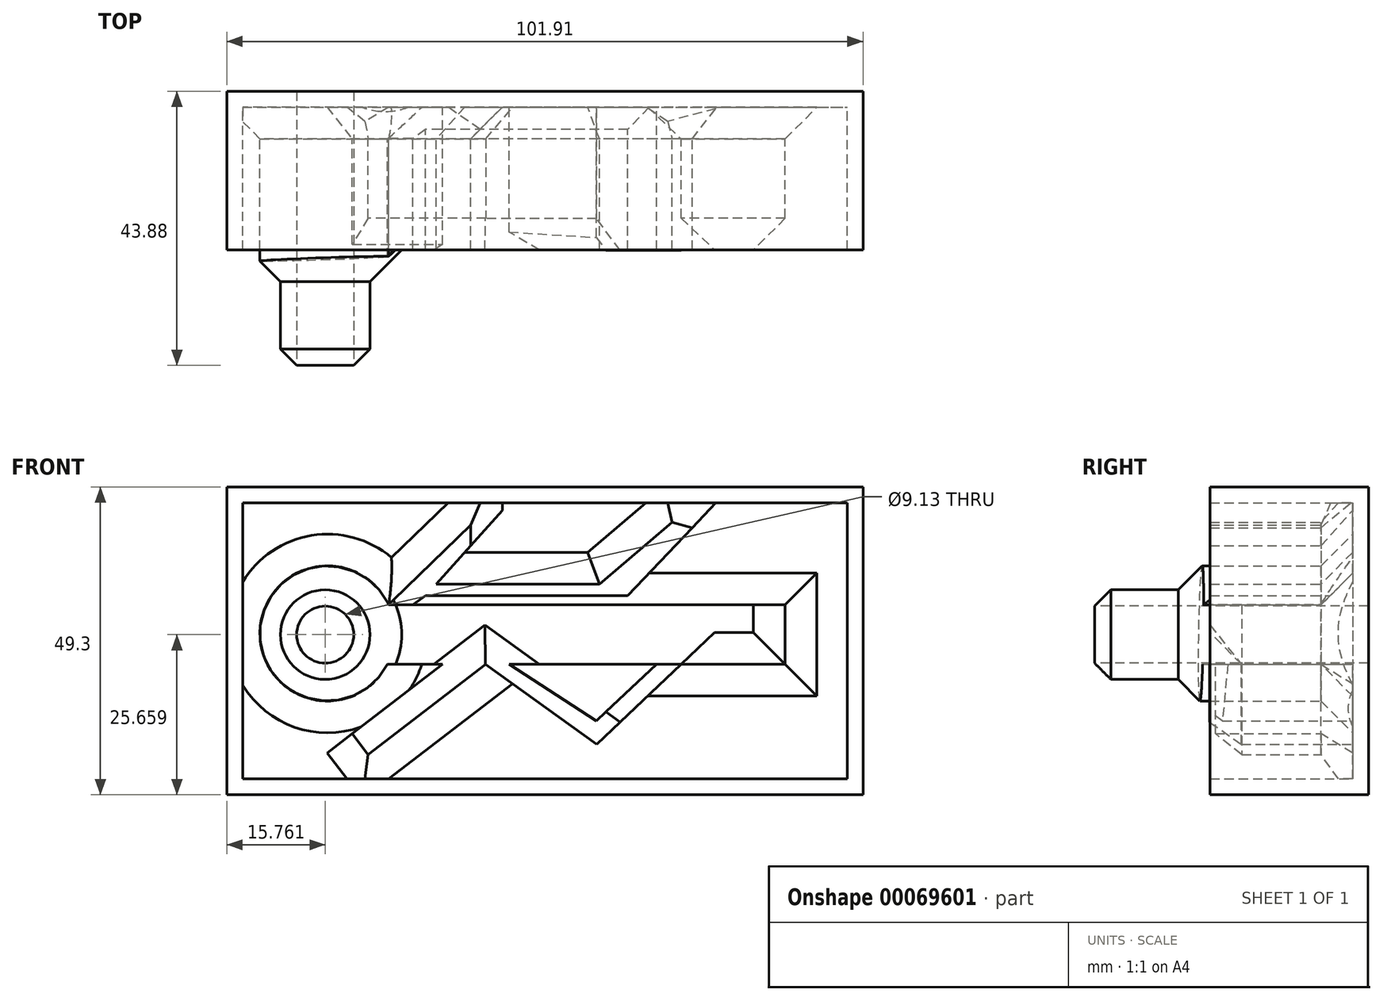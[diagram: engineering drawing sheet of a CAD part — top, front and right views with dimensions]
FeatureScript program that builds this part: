
annotation { "Feature Type Name" : "Feature", "Feature Type Description" : "" }
export const myFeature = defineFeature(function(context is Context, id is Id, definition is map)
    precondition{}
    {
        {
            var Q0;
            Q0=qCreatedBy(makeId("Front.planeOp"),FACE);
            var sketch = newSketch(context, id + "F0", { "sketchPlane" : qUnion([Q0])});
            skLineSegment(sketch, "E0.bottom", {"start": v(-39.04, 53.61) * mm, "end": v(62.87, 53.61) * mm});
            skLineSegment(sketch, "E0.top", {"start": v(-39.04, 4.3) * mm, "end": v(62.87, 4.3) * mm});
            skLineSegment(sketch, "E0.left", {"start": v(-39.04, 53.61) * mm, "end": v(-39.04, 4.3) * mm});
            skLineSegment(sketch, "E0.right", {"start": v(62.87, 53.61) * mm, "end": v(62.87, 4.3) * mm});
            skSolve(sketch);
        }
        {
            var Q0;
            Q0 = qSketchRegion(id + "F0", true);
            extrude(context, id + "F1", {"entities" : qUnion([Q0]), "depth" : 25.4 * mm});
        }
        {
            var Q0;
            Q0=makeQuery(id+"F1.opExtrude","CAP_FACE",FACE,{"disambiguationData":[OSD([sQuery(id+"F0.wireOp",EDGE,"E0.bottom"),sQuery(id+"F0.wireOp",EDGE,"E0.top"),sQuery(id+"F0.wireOp",EDGE,"E0.left"),sQuery(id+"F0.wireOp",EDGE,"E0.right")])],"isStart":false});
            shell(context, id + "F2", {"entities" : qUnion([Q0]), "thickness" : 2.54 * mm});
        }
        {
            var Q0;
            Q0=qCreatedBy(makeId("Front.planeOp"),FACE);
            var sketch = newSketch(context, id + "F3", { "sketchPlane" : qUnion([Q0])});
            skCircle(sketch, "E1", {"center": v(-22.91, 30.15) * mm, "radius": 10.83 * mm});
            skSolve(sketch);
        }
        {
            var Q0;
            Q0 = qSketchRegion(id + "F3", true);
            extrude(context, id + "F4", {"entities" : qUnion([Q0]), "operationType" : NewBodyOperationType.ADD, "depth" : 25.4 * mm});
        }
        {
            var Q0;
            Q0=qCreatedBy(makeId("Front.planeOp"),FACE);
            var sketch = newSketch(context, id + "F5", { "sketchPlane" : qUnion([Q0])});
            skLineSegment(sketch, "E2.bottom", {"start": v(-24.75, 34.74) * mm, "end": v(50.4, 34.74) * mm});
            skLineSegment(sketch, "E2.top", {"start": v(-24.75, 25.2) * mm, "end": v(50.4, 25.2) * mm});
            skLineSegment(sketch, "E2.left", {"start": v(-24.75, 34.74) * mm, "end": v(-24.75, 25.2) * mm});
            skLineSegment(sketch, "E2.right", {"start": v(50.4, 34.74) * mm, "end": v(50.4, 25.2) * mm});
            skSolve(sketch);
        }
        {
            var Q0;
            Q0 = qSketchRegion(id + "F5", true);
            extrude(context, id + "F6", {"entities" : qUnion([Q0]), "operationType" : NewBodyOperationType.ADD, "depth" : 25.4 * mm});
        }
        {
            var Q0;
            Q0=qCreatedBy(makeId("Front.planeOp"),FACE);
            var sketch = newSketch(context, id + "F7", { "sketchPlane" : qUnion([Q0])});
            skLineSegment(sketch, "E3", {"start": v(-4.39, 25.27) * mm, "end": v(-18.96, 14.09) * mm});
            skLineSegment(sketch, "E4", {"start": v(-18.96, 14.09) * mm, "end": v(-16.4, 10.74) * mm});
            skLineSegment(sketch, "E5", {"start": v(-16.4, 10.74) * mm, "end": v(2.46, 25.2) * mm});
            skLineSegment(sketch, "E6", {"start": v(2.46, 25.2) * mm, "end": v(-4.39, 25.27) * mm});
            skLineSegment(sketch, "E7", {"start": v(-4.39, 34.9) * mm, "end": v(-18.96, 47) * mm});
            skLineSegment(sketch, "E8", {"start": v(-18.96, 47) * mm, "end": v(-16.4, 50.08) * mm});
            skLineSegment(sketch, "E9", {"start": v(2.46, 34.9) * mm, "end": v(-16.4, 50.08) * mm});
            skSolve(sketch);
        }
        {
            var Q0;
            Q0 = qSketchRegion(id + "F7", true);
            extrude(context, id + "F8", {"entities" : qUnion([Q0]), "operationType" : NewBodyOperationType.ADD, "depth" : 25.4 * mm});
        }
        {
            var Q0;
            Q0=makeQuery(id+"F2.opShell","OFFSET_FACE",FACE,{"disambiguationData":[OSD([sQuery(id+"F0.wireOp",EDGE,"E0.bottom"),sQuery(id+"F0.wireOp",EDGE,"E0.top"),sQuery(id+"F0.wireOp",EDGE,"E0.left"),sQuery(id+"F0.wireOp",EDGE,"E0.right")])]});
            var sketch = newSketch(context, id + "F9", { "sketchPlane" : qUnion([Q0])});
            skLineSegment(sketch, "E10", {"start": v(2.45, 25.2) * mm, "end": v(20.2, 12.4) * mm});
            skLineSegment(sketch, "E11", {"start": v(20.2, 12.4) * mm, "end": v(33.74, 25.2) * mm});
            skLineSegment(sketch, "E12", {"start": v(33.74, 25.2) * mm, "end": v(29.83, 25.2) * mm});
            skLineSegment(sketch, "E13", {"start": v(29.83, 25.2) * mm, "end": v(20.18, 16.16) * mm});
            skLineSegment(sketch, "E14", {"start": v(20.18, 16.16) * mm, "end": v(6.16, 25.2) * mm});
            skLineSegment(sketch, "E15", {"start": v(6.16, 25.2) * mm, "end": v(2.45, 25.2) * mm});
            skSolve(sketch);
        }
        {
            var Q0;
            Q0=makeQuery(id+"F9.imprint","IMPRINT",FACE,{"disambiguationData":[TD([[makeQuery(id+"F9.imprint","IMPRINT",EDGE,{"derivedFrom":sQuery(id+"F9.wireOp",EDGE,"E10")}),1.0]])]});
            extrude(context, id + "F10", {"entities" : qUnion([Q0]), "operationType" : NewBodyOperationType.ADD, "depth" : 22.92 * mm});
        }
        {
            var Q0;
            Q0=qCreatedBy(makeId("Front.planeOp"),FACE);
            var sketch = newSketch(context, id + "F11", { "sketchPlane" : qUnion([Q0])});
            skCircle(sketch, "E16", {"center": v(-23.28, 29.97) * mm, "radius": 7.17 * mm});
            skSolve(sketch);
        }
        {
            var Q0;
            Q0 = qSketchRegion(id + "F11", true);
            extrude(context, id + "F12", {"entities" : qUnion([Q0]), "operationType" : NewBodyOperationType.ADD, "depth" : 46.36 * mm});
        }
        {
            var Q0;
            Q0=makeQuery(id+"F12.opExtrude","CAP_FACE",FACE,{"disambiguationData":[OSD([sQuery(id+"F11.wireOp",EDGE,"E16")])],"isStart":false});
            var sketch = newSketch(context, id + "F13", { "sketchPlane" : qUnion([Q0])});
            skCircle(sketch, "E17", {"center": v(-23.28, 29.97) * mm, "radius": 4.57 * mm});
            skSolve(sketch);
        }
        {
            var Q0;
            Q0 = qSketchRegion(id + "F13", true);
            extrude(context, id + "F14", {"entities" : qUnion([Q0]), "operationType" : NewBodyOperationType.REMOVE, "oppositeDirection" : true, "depth" : 82.72 * mm});
        }
        {
            var Q0;
            Q0=qCreatedBy(makeId("Front.planeOp"),FACE);
            var sketch = newSketch(context, id + "F15", { "sketchPlane" : qUnion([Q0])});
            skLineSegment(sketch, "E18", {"start": v(33.75, 25.15) * mm, "end": v(45.4, 12.34) * mm});
            skLineSegment(sketch, "E19", {"start": v(45.4, 12.34) * mm, "end": v(48.04, 14.74) * mm});
            skLineSegment(sketch, "E20", {"start": v(48.04, 14.74) * mm, "end": v(38.76, 24.95) * mm});
            skLineSegment(sketch, "E21", {"start": v(38.76, 24.95) * mm, "end": v(45.7, 24.95) * mm});
            skLineSegment(sketch, "E22", {"start": v(45.7, 24.95) * mm, "end": v(54.62, 13.5) * mm});
            skLineSegment(sketch, "E23", {"start": v(54.62, 13.5) * mm, "end": v(54.62, 44.87) * mm});
            skLineSegment(sketch, "E24", {"start": v(54.62, 44.87) * mm, "end": v(45.7, 34.86) * mm});
            skLineSegment(sketch, "E25", {"start": v(45.7, 34.86) * mm, "end": v(38.76, 34.86) * mm});
            skLineSegment(sketch, "E26", {"start": v(38.76, 34.86) * mm, "end": v(46.45, 43.47) * mm});
            skLineSegment(sketch, "E27", {"start": v(46.45, 43.47) * mm, "end": v(42.4, 44.96) * mm});
            skLineSegment(sketch, "E28", {"start": v(42.4, 44.96) * mm, "end": v(33.75, 34.77) * mm});
            skLineSegment(sketch, "E29", {"start": v(33.75, 34.77) * mm, "end": v(-13.15, 34.77) * mm});
            skLineSegment(sketch, "E30", {"start": v(-13.15, 34.77) * mm, "end": v(0, 47.49) * mm});
            skLineSegment(sketch, "E31", {"start": v(0, 47.49) * mm, "end": v(0, 44.19) * mm});
            skLineSegment(sketch, "E32", {"start": v(0, 44.19) * mm, "end": v(-5.48, 38.07) * mm});
            skLineSegment(sketch, "E33", {"start": v(-5.48, 38.07) * mm, "end": v(20.64, 38.07) * mm});
            skLineSegment(sketch, "E34", {"start": v(20.64, 38.07) * mm, "end": v(32.3, 47.97) * mm});
            skLineSegment(sketch, "E35", {"start": v(32.3, 47.97) * mm, "end": v(35.5, 47.1) * mm});
            skLineSegment(sketch, "E36", {"start": v(35.5, 47.1) * mm, "end": v(25.2, 36.22) * mm});
            skLineSegment(sketch, "E37", {"start": v(25.2, 36.22) * mm, "end": v(-7.23, 36.22) * mm});
            skLineSegment(sketch, "E38", {"start": v(-7.23, 36.22) * mm, "end": v(-9.27, 34.77) * mm});
            skLineSegment(sketch, "E39", {"start": v(-9.27, 34.77) * mm, "end": v(-13.15, 34.77) * mm});
            skSolve(sketch);
        }
        {
            var Q0;
            Q0 = qSketchRegion(id + "F15", true);
            extrude(context, id + "F16", {"entities" : qUnion([Q0]), "operationType" : NewBodyOperationType.ADD, "depth" : 25.4 * mm});
        }
        {
            var Q0;
            Q0=makeQuery(id+"F12.boolean.opBoolean","INTERSECT",EDGE,{"derivedFrom":[makeQuery(id+"F8.boolean.opBoolean","MERGE",FACE,{"derivedFrom":[makeQuery(id+"F6.boolean.opBoolean","MERGE",FACE,{"derivedFrom":[makeQuery(id+"F4.opExtrude","CAP_FACE",FACE,{"disambiguationData":[OSD([sQuery(id+"F3.wireOp",EDGE,"E1")])],"isStart":false}),makeQuery(id+"F6.opExtrude","CAP_FACE",FACE,{"disambiguationData":[OSD([sQuery(id+"F5.wireOp",EDGE,"E2.bottom"),sQuery(id+"F5.wireOp",EDGE,"E2.top"),sQuery(id+"F5.wireOp",EDGE,"E2.left"),sQuery(id+"F5.wireOp",EDGE,"E2.right")])],"isStart":false})]}),makeQuery(id+"F8.opExtrude","CAP_FACE",FACE,{"disambiguationData":[OSD([sQuery(id+"F7.wireOp",EDGE,"E3"),sQuery(id+"F7.wireOp",EDGE,"E4"),sQuery(id+"F7.wireOp",EDGE,"E5"),sQuery(id+"F7.wireOp",EDGE,"E6")])],"isStart":false})]}),makeQuery(id+"F12.opExtrude","SWEPT_FACE",FACE,{"disambiguationData":[OSD([sQuery(id+"F11.wireOp",EDGE,"E16")])]})]});
            var Q1;
            Q1=makeQuery(id+"F12.opExtrude","CAP_EDGE",EDGE,{"disambiguationData":[OSD([sQuery(id+"F11.wireOp",EDGE,"E16")])],"isStart":false});
            var Q2;
            {var subQ0=makeQuery(id+"F2.opShell","OFFSET_FACE",FACE,{"disambiguationData":[OSD([sQuery(id+"F0.wireOp",EDGE,"E0.bottom"),sQuery(id+"F0.wireOp",EDGE,"E0.top"),sQuery(id+"F0.wireOp",EDGE,"E0.left"),sQuery(id+"F0.wireOp",EDGE,"E0.right")])]});var subQ1=makeQuery(id+"F4.opExtrude","SWEPT_FACE",FACE,{"disambiguationData":[OSD([sQuery(id+"F3.wireOp",EDGE,"E1")])]});Q2=makeQuery(id+"F16.boolean.opBoolean","SPLIT",EDGE,{"disambiguationData":[TD([makeQuery(id+"F6.opExtrude","SWEPT_FACE",FACE,{"disambiguationData":[OSD([sQuery(id+"F5.wireOp",EDGE,"E2.top")])]})])],"derivedFrom":makeQuery(id+"F4.boolean.opBoolean","INTERSECT",EDGE,{"derivedFrom":[subQ0,subQ1]})});}
            var Q3;
            Q3=makeQuery(id+"F8.opExtrude","CAP_EDGE",EDGE,{"disambiguationData":[OSD([sQuery(id+"F7.wireOp",EDGE,"E5")])],"isStart":false});
            var Q4;
            Q4=makeQuery(id+"F10.opExtrude","CAP_EDGE",EDGE,{"disambiguationData":[OSD([sQuery(id+"F9.wireOp",EDGE,"E10")])],"isStart":false});
            var Q5;
            {var subQ0=sQuery(id+"F5.wireOp",EDGE,"E2.top");var subQ1=makeQuery(id+"F6.opExtrude","SWEPT_FACE",FACE,{"disambiguationData":[OSD([subQ0])]});var subQ2=sQuery(id+"F5.wireOp",EDGE,"E2.right");var subQ3=makeQuery(id+"F6.opExtrude","CAP_FACE",FACE,{"disambiguationData":[OSD([sQuery(id+"F5.wireOp",EDGE,"E2.bottom"),subQ0,sQuery(id+"F5.wireOp",EDGE,"E2.left"),subQ2])],"isStart":false});var subQ4=makeQuery(id+"F6.opExtrude","SWEPT_FACE",FACE,{"disambiguationData":[OSD([subQ2])]});var subQ5=makeQuery(id+"F4.opExtrude","CAP_FACE",FACE,{"disambiguationData":[OSD([sQuery(id+"F3.wireOp",EDGE,"E1")])],"isStart":false});var subQ6=sQuery(id+"F7.wireOp",EDGE,"E5");var subQ7=makeQuery(id+"F8.opExtrude","CAP_FACE",FACE,{"disambiguationData":[OSD([sQuery(id+"F7.wireOp",EDGE,"E3"),sQuery(id+"F7.wireOp",EDGE,"E4"),subQ6,sQuery(id+"F7.wireOp",EDGE,"E6")])],"isStart":false});Q5=makeQuery(id+"F10.boolean.opBoolean","SPLIT",EDGE,{"disambiguationData":[TD([subQ5,subQ3,subQ1,subQ4,subQ7,makeQuery(id+"F10.opExtrude","SWEPT_FACE",FACE,{"disambiguationData":[OSD([sQuery(id+"F9.wireOp",EDGE,"E11")])]}),makeQuery(id+"F10.opExtrude","SWEPT_FACE",FACE,{"disambiguationData":[OSD([sQuery(id+"F9.wireOp",EDGE,"E12")])]})])],"derivedFrom":makeQuery(id+"F8.boolean.opBoolean","SPLIT",EDGE,{"disambiguationData":[TD([subQ4])],"derivedFrom":makeQuery(id+"F6.opExtrude","CAP_EDGE",EDGE,{"disambiguationData":[OSD([subQ0])],"isStart":false})})});}
            var Q6;
            Q6=makeQuery(id+"F6.opExtrude","CAP_EDGE",EDGE,{"disambiguationData":[OSD([sQuery(id+"F5.wireOp",EDGE,"E2.right")])],"isStart":false});
            var Q7;
            Q7=makeQuery(id+"F10.opExtrude","CAP_EDGE",EDGE,{"disambiguationData":[OSD([sQuery(id+"F9.wireOp",EDGE,"E11")])],"isStart":true});
            var Q8;
            {var subQ0=sQuery(id+"F0.wireOp",EDGE,"E0.bottom");var subQ1=sQuery(id+"F0.wireOp",EDGE,"E0.top");var subQ2=sQuery(id+"F0.wireOp",EDGE,"E0.left");var subQ3=sQuery(id+"F0.wireOp",EDGE,"E0.right");Q8=makeQuery(id+"F16.boolean.opBoolean","INTERSECT",EDGE,{"derivedFrom":[makeQuery(id+"F10.boolean.opBoolean","SPLIT",FACE,{"disambiguationData":[TD([makeQuery(id+"F2.opShell","OFFSET_FACE",FACE,{"disambiguationData":[OSD([subQ0])]})])],"derivedFrom":makeQuery(id+"F2.opShell","OFFSET_FACE",FACE,{"disambiguationData":[OSD([subQ0,subQ1,subQ2,subQ3])]})}),makeQuery(id+"F16.opExtrude","SWEPT_FACE",FACE,{"disambiguationData":[OSD([sQuery(id+"F15.wireOp",EDGE,"E33")])]})]});}
            var Q9;
            Q9=makeQuery(id+"F6.boolean.opBoolean","INTERSECT",EDGE,{"derivedFrom":[makeQuery(id+"F2.opShell","OFFSET_FACE",FACE,{"disambiguationData":[OSD([sQuery(id+"F0.wireOp",EDGE,"E0.bottom"),sQuery(id+"F0.wireOp",EDGE,"E0.top"),sQuery(id+"F0.wireOp",EDGE,"E0.left"),sQuery(id+"F0.wireOp",EDGE,"E0.right")])]}),makeQuery(id+"F6.opExtrude","SWEPT_FACE",FACE,{"disambiguationData":[OSD([sQuery(id+"F5.wireOp",EDGE,"E2.bottom")])]})]});
            var Q10;
            Q10=makeQuery(id+"F6.boolean.opBoolean","INTERSECT",EDGE,{"derivedFrom":[makeQuery(id+"F2.opShell","OFFSET_FACE",FACE,{"disambiguationData":[OSD([sQuery(id+"F0.wireOp",EDGE,"E0.bottom"),sQuery(id+"F0.wireOp",EDGE,"E0.top"),sQuery(id+"F0.wireOp",EDGE,"E0.left"),sQuery(id+"F0.wireOp",EDGE,"E0.right")])]}),makeQuery(id+"F6.opExtrude","SWEPT_FACE",FACE,{"disambiguationData":[OSD([sQuery(id+"F5.wireOp",EDGE,"E2.right")])]})]});
            var Q11;
            {var subQ0=makeQuery(id+"F2.opShell","OFFSET_FACE",FACE,{"disambiguationData":[OSD([sQuery(id+"F0.wireOp",EDGE,"E0.bottom"),sQuery(id+"F0.wireOp",EDGE,"E0.top"),sQuery(id+"F0.wireOp",EDGE,"E0.left"),sQuery(id+"F0.wireOp",EDGE,"E0.right")])]});var subQ1=makeQuery(id+"F6.opExtrude","SWEPT_FACE",FACE,{"disambiguationData":[OSD([sQuery(id+"F5.wireOp",EDGE,"E2.top")])]});var subQ2=makeQuery(id+"F6.opExtrude","SWEPT_FACE",FACE,{"disambiguationData":[OSD([sQuery(id+"F5.wireOp",EDGE,"E2.right")])]});Q11=makeQuery(id+"F10.boolean.opBoolean","SPLIT",EDGE,{"disambiguationData":[TD([subQ2])],"derivedFrom":makeQuery(id+"F8.boolean.opBoolean","SPLIT",EDGE,{"disambiguationData":[TD([subQ2])],"derivedFrom":makeQuery(id+"F6.boolean.opBoolean","INTERSECT",EDGE,{"derivedFrom":[subQ0,subQ1]})})});}
            var Q12;
            Q12=makeQuery(id+"F10.opExtrude","CAP_EDGE",EDGE,{"disambiguationData":[OSD([sQuery(id+"F9.wireOp",EDGE,"E10")])],"isStart":true});
            var Q13;
            Q13=makeQuery(id+"F8.boolean.opBoolean","INTERSECT",EDGE,{"derivedFrom":[makeQuery(id+"F2.opShell","OFFSET_FACE",FACE,{"disambiguationData":[OSD([sQuery(id+"F0.wireOp",EDGE,"E0.bottom"),sQuery(id+"F0.wireOp",EDGE,"E0.top"),sQuery(id+"F0.wireOp",EDGE,"E0.left"),sQuery(id+"F0.wireOp",EDGE,"E0.right")])]}),makeQuery(id+"F8.opExtrude","SWEPT_FACE",FACE,{"disambiguationData":[OSD([sQuery(id+"F7.wireOp",EDGE,"E5")])]})]});
            var Q14;
            Q14=makeQuery(id+"F8.boolean.opBoolean","INTERSECT",EDGE,{"derivedFrom":[makeQuery(id+"F2.opShell","OFFSET_FACE",FACE,{"disambiguationData":[OSD([sQuery(id+"F0.wireOp",EDGE,"E0.bottom"),sQuery(id+"F0.wireOp",EDGE,"E0.top"),sQuery(id+"F0.wireOp",EDGE,"E0.left"),sQuery(id+"F0.wireOp",EDGE,"E0.right")])]}),makeQuery(id+"F8.opExtrude","SWEPT_FACE",FACE,{"disambiguationData":[OSD([sQuery(id+"F7.wireOp",EDGE,"E4")])]})]});
            var Q15;
            {var subQ0=sQuery(id+"F0.wireOp",EDGE,"E0.bottom");var subQ1=sQuery(id+"F0.wireOp",EDGE,"E0.top");var subQ2=sQuery(id+"F0.wireOp",EDGE,"E0.left");var subQ3=sQuery(id+"F0.wireOp",EDGE,"E0.right");Q15=makeQuery(id+"F16.boolean.opBoolean","INTERSECT",EDGE,{"derivedFrom":[makeQuery(id+"F10.boolean.opBoolean","SPLIT",FACE,{"disambiguationData":[TD([makeQuery(id+"F2.opShell","OFFSET_FACE",FACE,{"disambiguationData":[OSD([subQ0])]})])],"derivedFrom":makeQuery(id+"F2.opShell","OFFSET_FACE",FACE,{"disambiguationData":[OSD([subQ0,subQ1,subQ2,subQ3])]})}),makeQuery(id+"F16.opExtrude","SWEPT_FACE",FACE,{"disambiguationData":[OSD([sQuery(id+"F15.wireOp",EDGE,"E30")])]})]});}
            var Q16;
            {var subQ0=sQuery(id+"F0.wireOp",EDGE,"E0.bottom");var subQ1=sQuery(id+"F0.wireOp",EDGE,"E0.top");var subQ2=sQuery(id+"F0.wireOp",EDGE,"E0.left");var subQ3=sQuery(id+"F0.wireOp",EDGE,"E0.right");Q16=makeQuery(id+"F16.boolean.opBoolean","INTERSECT",EDGE,{"derivedFrom":[makeQuery(id+"F10.boolean.opBoolean","SPLIT",FACE,{"disambiguationData":[TD([makeQuery(id+"F2.opShell","OFFSET_FACE",FACE,{"disambiguationData":[OSD([subQ0])]})])],"derivedFrom":makeQuery(id+"F2.opShell","OFFSET_FACE",FACE,{"disambiguationData":[OSD([subQ0,subQ1,subQ2,subQ3])]})}),makeQuery(id+"F16.opExtrude","SWEPT_FACE",FACE,{"disambiguationData":[OSD([sQuery(id+"F15.wireOp",EDGE,"E31")])]})]});}
            var Q17;
            {var subQ0=sQuery(id+"F0.wireOp",EDGE,"E0.bottom");var subQ1=sQuery(id+"F0.wireOp",EDGE,"E0.top");var subQ2=sQuery(id+"F0.wireOp",EDGE,"E0.left");var subQ3=sQuery(id+"F0.wireOp",EDGE,"E0.right");Q17=makeQuery(id+"F16.boolean.opBoolean","INTERSECT",EDGE,{"derivedFrom":[makeQuery(id+"F10.boolean.opBoolean","SPLIT",FACE,{"disambiguationData":[TD([makeQuery(id+"F2.opShell","OFFSET_FACE",FACE,{"disambiguationData":[OSD([subQ0])]})])],"derivedFrom":makeQuery(id+"F2.opShell","OFFSET_FACE",FACE,{"disambiguationData":[OSD([subQ0,subQ1,subQ2,subQ3])]})}),makeQuery(id+"F16.opExtrude","SWEPT_FACE",FACE,{"disambiguationData":[OSD([sQuery(id+"F15.wireOp",EDGE,"E34")])]})]});}
            var Q18;
            {var subQ0=sQuery(id+"F0.wireOp",EDGE,"E0.bottom");var subQ1=sQuery(id+"F0.wireOp",EDGE,"E0.top");var subQ2=sQuery(id+"F0.wireOp",EDGE,"E0.left");var subQ3=sQuery(id+"F0.wireOp",EDGE,"E0.right");Q18=makeQuery(id+"F16.boolean.opBoolean","INTERSECT",EDGE,{"derivedFrom":[makeQuery(id+"F10.boolean.opBoolean","SPLIT",FACE,{"disambiguationData":[TD([makeQuery(id+"F2.opShell","OFFSET_FACE",FACE,{"disambiguationData":[OSD([subQ0])]})])],"derivedFrom":makeQuery(id+"F2.opShell","OFFSET_FACE",FACE,{"disambiguationData":[OSD([subQ0,subQ1,subQ2,subQ3])]})}),makeQuery(id+"F16.opExtrude","SWEPT_FACE",FACE,{"disambiguationData":[OSD([sQuery(id+"F15.wireOp",EDGE,"E35")])]})]});}
            chamfer(context, id + "F17", {"entities" : qUnion([Q0, Q1, Q2, Q3, Q4, Q5, Q6, Q7, Q8, Q9, Q10, Q11, Q12, Q13, Q14, Q15, Q16, Q17, Q18]), "width" : 5.08 * mm, "tangentPropagation" : true});
        }
    });
